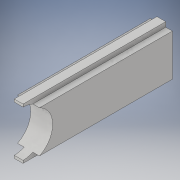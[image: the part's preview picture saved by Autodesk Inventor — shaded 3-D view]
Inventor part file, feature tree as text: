
AUTODESK INVENTOR PART (.ipt)
format: ipt  version: 2018 (Build 220112000, 112)  size: 122,880 bytes
history: native  units: in
note: dims shown in document units (in); Inventor stores cm internally (conversion verified against a paired STEP export)
features: extrude x2, sketch x1
ambient origin geometry x8: Origin, YZ Plane, XZ Plane, XY Plane, X Axis, Y Axis, Z Axis, Center Point
bodies: Solid1 (feature_tree)
feature tree (3):
  extrude  "Extrusion1"  Depth=0.95in
  extrude  "Extrusion2"  Depth=0.2in
  sketch  "Sketch2"  dims[d0=0.5in d1=0.95in d2=0.2in d3=0.11in d4=0.15in d5=0.2in d6=0.11in d7=0.15in d8=3.25in d9=0.0in d10=1.05in d11=3.25in d12=0.0in]
